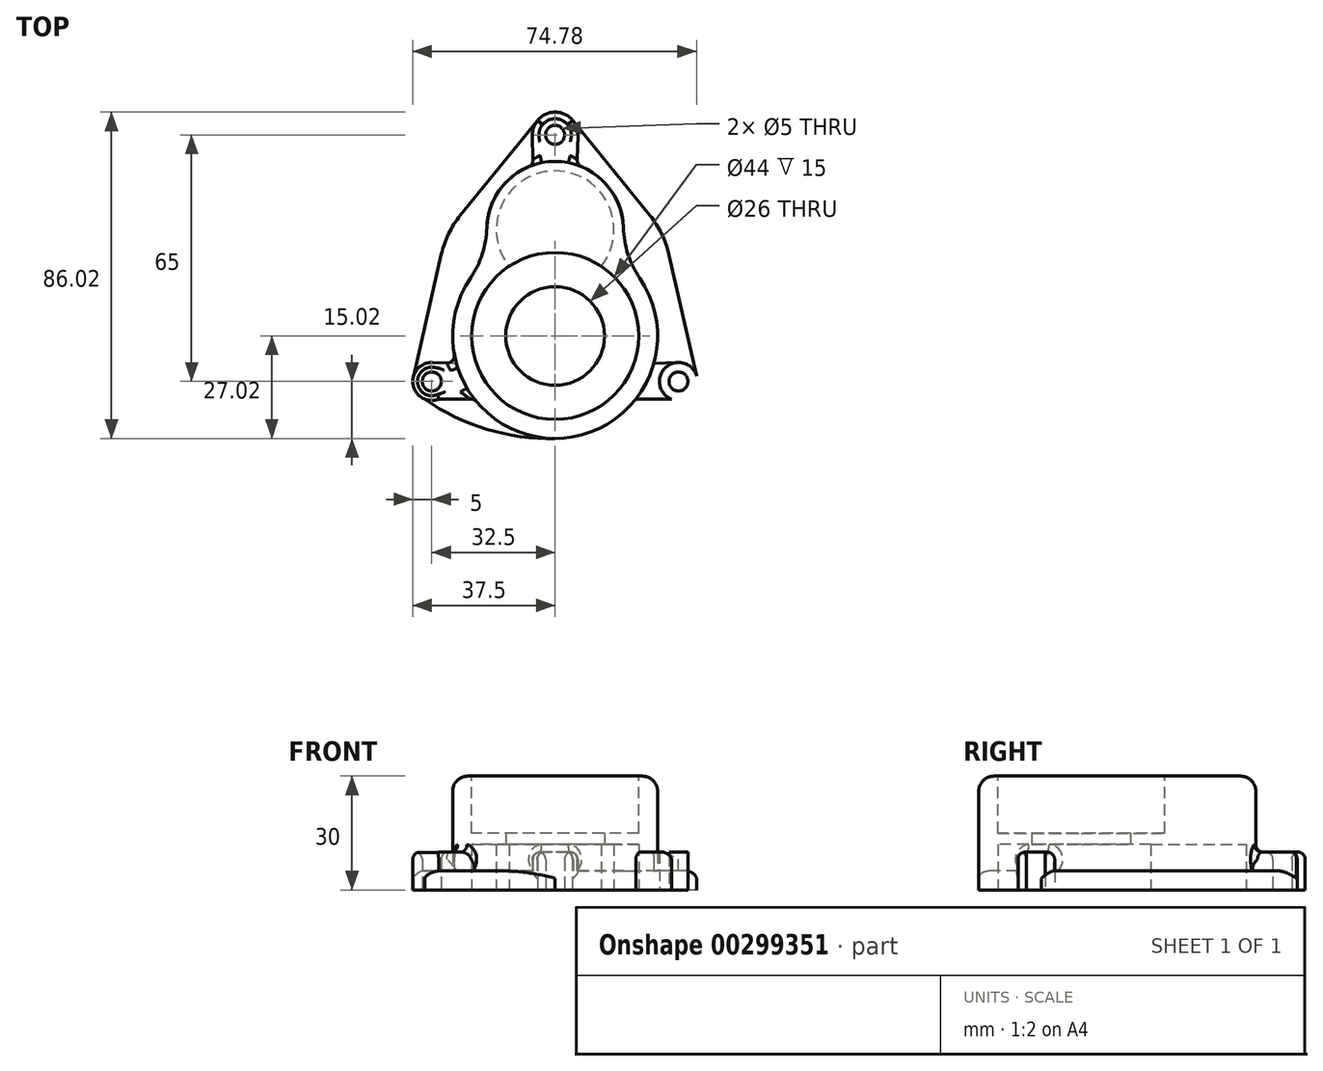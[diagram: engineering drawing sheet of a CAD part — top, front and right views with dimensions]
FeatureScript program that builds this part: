
annotation { "Feature Type Name" : "Feature", "Feature Type Description" : "" }
export const myFeature = defineFeature(function(context is Context, id is Id, definition is map)
    precondition{}
    {
        {
            var Q0;
            Q0=qCreatedBy(makeId("Top.planeOp"),FACE);
            var sketch = newSketch(context, id + "F0", { "sketchPlane" : qUnion([Q0])});
            skCircle(sketch, "E0", {"center": v(0, 0) * mm, "radius": 13 * mm});
            skCircle(sketch, "E1", {"center": v(0, 0) * mm, "radius": 22 * mm});
            skCircle(sketch, "E2", {"center": v(0, 0) * mm, "radius": 27 * mm});
            skPoint(sketch, "E3", {"position": v(32.5, -12) * mm});
            skPoint(sketch, "E4.MirrorP", {"position": v(-32.5, -12) * mm});
            skCircle(sketch, "E5", {"center": v(-32.5, -12) * mm, "radius": 2.5 * mm});
            skCircle(sketch, "E6.MirrorC", {"center": v(32.5, -12) * mm, "radius": 2.5 * mm});
            skPoint(sketch, "E7", {"position": v(0, 46) * mm});
            skPoint(sketch, "E8", {"position": v(0, 28) * mm});
            skLineSegment(sketch, "E9", {"start": v(-32.5, -12) * mm, "end": v(32.5, -12) * mm});
            skArc(sketch, "E10", {"start": v(16.68, 21.23) * mm, "mid": v(0, 46) * mm, "end": v(-16.68, 21.23) * mm});
            skCircle(sketch, "E11", {"center": v(0, 28) * mm, "radius": 15.5 * mm});
            skPoint(sketch, "E12", {"position": v(5.58, 15.98) * mm});
            skPoint(sketch, "E13", {"position": v(27.5, 28) * mm});
            skPoint(sketch, "E14.MirrorP", {"position": v(-5.58, 15.98) * mm});
            skPoint(sketch, "E15.MirrorP", {"position": v(-27.5, 28) * mm});
            skArc(sketch, "E16", {"start": v(29.95, 21.55) * mm, "mid": v(28.06, 26.93) * mm, "end": v(24.99, 31.74) * mm});
            skArc(sketch, "E17", {"start": v(-24.99, 31.74) * mm, "mid": v(-28.06, 26.93) * mm, "end": v(-29.95, 21.55) * mm});
            skPoint(sketch, "E18", {"position": v(0, 53) * mm});
            skCircle(sketch, "E19", {"center": v(0, 53) * mm, "radius": 6 * mm});
            skLineSegment(sketch, "E20", {"start": v(-6, 52.83) * mm, "end": v(-5.78, 45.05) * mm});
            skLineSegment(sketch, "E21.MirrorCS", {"start": v(6, 52.83) * mm, "end": v(5.78, 45.05) * mm});
            skLineSegment(sketch, "E22", {"start": v(-4.58, 56.88) * mm, "end": v(-24.99, 31.74) * mm});
            skLineSegment(sketch, "E23.MirrorCS", {"start": v(4.58, 56.88) * mm, "end": v(24.99, 31.74) * mm});
            skCircle(sketch, "E24", {"center": v(-32.5, -12) * mm, "radius": 5 * mm});
            skLineSegment(sketch, "E25", {"start": v(-37.28, -10.54) * mm, "end": v(-29.95, 21.55) * mm});
            skLineSegment(sketch, "E26.MirrorCS", {"start": v(37.28, -10.54) * mm, "end": v(29.95, 21.55) * mm});
            skCircle(sketch, "E27.MirrorC", {"center": v(32.5, -12) * mm, "radius": 5 * mm});
            skArc(sketch, "E28", {"start": v(-34.3, -16.66) * mm, "mid": v(-17.99, -24.6) * mm, "end": v(0, -27) * mm});
            skArc(sketch, "E29.MirrorCS", {"start": v(34.3, -16.66) * mm, "mid": v(17.99, -24.6) * mm, "end": v(0, -27) * mm});
            skCircle(sketch, "E30", {"center": v(0, 53) * mm, "radius": 2.5 * mm});
            skLineSegment(sketch, "E31", {"start": v(-32.34, -7) * mm, "end": v(-26.02, -7.2) * mm});
            skLineSegment(sketch, "E32", {"start": v(-34.3, -16.66) * mm, "end": v(-21.25, -16.66) * mm});
            skLineSegment(sketch, "E33.MirrorCS", {"start": v(32.34, -7) * mm, "end": v(26.02, -7.2) * mm});
            skLineSegment(sketch, "E34.MirrorCS", {"start": v(34.3, -16.66) * mm, "end": v(21.25, -16.66) * mm});
            skSolve(sketch);
        }
        {
            var Q0;
            {var subQ0=sQuery(id+"F0.wireOp",EDGE,"E11");var subQ1=sQuery(id+"F0.wireOp",EDGE,"E2");var subQ2=makeQuery(id+"F0.imprint","INTERSECT",VERTEX,{"disambiguationData":[OD(0.0)],"derivedFrom":[subQ1,subQ0]});Q0=makeQuery(id+"F0.imprint","IMPRINT",FACE,{"disambiguationData":[TD([[makeQuery(id+"F0.imprint","IMPRINT",EDGE,{"disambiguationData":[TD([[subQ2,-1.0]])],"derivedFrom":subQ1}),-1.0]])]});}
            var Q1;
            {var subQ0=sQuery(id+"F0.wireOp",EDGE,"E10");var subQ1=sQuery(id+"F0.wireOp",EDGE,"E2");var subQ2=makeQuery(id+"F0.imprint","INTERSECT",VERTEX,{"disambiguationData":[OD(0.0)],"derivedFrom":[subQ1,subQ0]});Q1=makeQuery(id+"F0.imprint","IMPRINT",FACE,{"disambiguationData":[TD([[makeQuery(id+"F0.imprint","IMPRINT",EDGE,{"disambiguationData":[TD([[subQ2,-1.0]])],"derivedFrom":subQ1}),-1.0]])]});}
            var Q2;
            {var subQ0=sQuery(id+"F0.wireOp",EDGE,"E11");var subQ1=sQuery(id+"F0.wireOp",EDGE,"E1");var subQ2=makeQuery(id+"F0.imprint","INTERSECT",VERTEX,{"disambiguationData":[OD(0.0)],"derivedFrom":[subQ1,subQ0]});Q2=makeQuery(id+"F0.imprint","IMPRINT",FACE,{"disambiguationData":[TD([[makeQuery(id+"F0.imprint","IMPRINT",EDGE,{"disambiguationData":[TD([[subQ2,1.0]])],"derivedFrom":subQ1}),-1.0]])]});}
            var Q3;
            {var subQ0=sQuery(id+"F0.wireOp",EDGE,"E11");var subQ1=sQuery(id+"F0.wireOp",EDGE,"E0");var subQ2=makeQuery(id+"F0.imprint","INTERSECT",VERTEX,{"disambiguationData":[OD(0.0)],"derivedFrom":[subQ1,subQ0]});Q3=makeQuery(id+"F0.imprint","IMPRINT",FACE,{"disambiguationData":[TD([[makeQuery(id+"F0.imprint","IMPRINT",EDGE,{"disambiguationData":[TD([[subQ2,1.0]])],"derivedFrom":subQ1}),-1.0]])]});}
            var Q4;
            {var subQ4=sQuery(id+"F0.wireOp",EDGE,"E11");var subQ6=sQuery(id+"F0.wireOp",EDGE,"E1");var subQ8=makeQuery(id+"F0.imprint","INTERSECT",VERTEX,{"disambiguationData":[OD(1.0)],"derivedFrom":[subQ6,subQ4]});Q4=makeQuery(id+"F0.imprint","IMPRINT",FACE,{"disambiguationData":[TD([[makeQuery(id+"F0.imprint","IMPRINT",EDGE,{"disambiguationData":[TD([[subQ8,1.0]])],"derivedFrom":subQ6}),-1.0]])]});}
            var Q5;
            {var subQ1=sQuery(id+"F0.wireOp",EDGE,"E1");var subQ6=sQuery(id+"F0.wireOp",EDGE,"E11");var subQ8=makeQuery(id+"F0.imprint","INTERSECT",VERTEX,{"disambiguationData":[OD(0.0)],"derivedFrom":[subQ1,subQ6]});Q5=makeQuery(id+"F0.imprint","IMPRINT",FACE,{"disambiguationData":[TD([[makeQuery(id+"F0.imprint","IMPRINT",EDGE,{"disambiguationData":[TD([[subQ8,-1.0]])],"derivedFrom":subQ1}),-1.0]])]});}
            var Q6;
            {var subQ0=sQuery(id+"F0.wireOp",EDGE,"E11");var subQ1=sQuery(id+"F0.wireOp",EDGE,"E0");var subQ2=makeQuery(id+"F0.imprint","INTERSECT",VERTEX,{"disambiguationData":[OD(0.0)],"derivedFrom":[subQ1,subQ0]});Q6=makeQuery(id+"F0.imprint","IMPRINT",FACE,{"disambiguationData":[TD([[makeQuery(id+"F0.imprint","IMPRINT",EDGE,{"disambiguationData":[TD([[subQ2,-1.0]])],"derivedFrom":subQ1}),-1.0]])]});}
            var Q7;
            {var subQ0=sQuery(id+"F0.wireOp",EDGE,"E11");var subQ1=sQuery(id+"F0.wireOp",EDGE,"E0");var subQ2=makeQuery(id+"F0.imprint","INTERSECT",VERTEX,{"disambiguationData":[OD(1.0)],"derivedFrom":[subQ1,subQ0]});Q7=makeQuery(id+"F0.imprint","IMPRINT",FACE,{"disambiguationData":[TD([[makeQuery(id+"F0.imprint","IMPRINT",EDGE,{"disambiguationData":[TD([[subQ2,1.0]])],"derivedFrom":subQ1}),-1.0]])]});}
            var Q8;
            {var subQ0=sQuery(id+"F0.wireOp",EDGE,"E11");var subQ1=sQuery(id+"F0.wireOp",EDGE,"E0");var subQ2=makeQuery(id+"F0.imprint","INTERSECT",VERTEX,{"disambiguationData":[OD(0.0)],"derivedFrom":[subQ1,subQ0]});Q8=makeQuery(id+"F0.imprint","IMPRINT",FACE,{"disambiguationData":[TD([[makeQuery(id+"F0.imprint","IMPRINT",EDGE,{"disambiguationData":[TD([[subQ2,-1.0]])],"derivedFrom":subQ1}),1.0]])]});}
            var Q9;
            {var subQ0=sQuery(id+"F0.wireOp",EDGE,"E9");var subQ1=sQuery(id+"F0.wireOp",EDGE,"E0");var subQ2=makeQuery(id+"F0.imprint","INTERSECT",VERTEX,{"disambiguationData":[OD(0.0)],"derivedFrom":[subQ1,subQ0]});Q9=makeQuery(id+"F0.imprint","IMPRINT",FACE,{"disambiguationData":[TD([[makeQuery(id+"F0.imprint","IMPRINT",EDGE,{"disambiguationData":[TD([[subQ2,-1.0]])],"derivedFrom":subQ1}),-1.0]])]});}
            var Q10;
            {var subQ0=sQuery(id+"F0.wireOp",EDGE,"E9");var subQ1=sQuery(id+"F0.wireOp",EDGE,"E1");var subQ2=makeQuery(id+"F0.imprint","INTERSECT",VERTEX,{"disambiguationData":[OD(0.0)],"derivedFrom":[subQ1,subQ0]});Q10=makeQuery(id+"F0.imprint","IMPRINT",FACE,{"disambiguationData":[TD([[makeQuery(id+"F0.imprint","IMPRINT",EDGE,{"disambiguationData":[TD([[subQ2,-1.0]])],"derivedFrom":subQ1}),-1.0]])]});}
            var Q11;
            {var subQ0=sQuery(id+"F0.wireOp",EDGE,"E9");var subQ1=sQuery(id+"F0.wireOp",EDGE,"E0");var subQ2=makeQuery(id+"F0.imprint","INTERSECT",VERTEX,{"disambiguationData":[OD(0.0)],"derivedFrom":[subQ1,subQ0]});Q11=makeQuery(id+"F0.imprint","IMPRINT",FACE,{"disambiguationData":[TD([[makeQuery(id+"F0.imprint","IMPRINT",EDGE,{"disambiguationData":[TD([[subQ2,-1.0]])],"derivedFrom":subQ1}),1.0]])]});}
            var Q12;
            {var subQ0=sQuery(id+"F0.wireOp",EDGE,"E11");var subQ1=sQuery(id+"F0.wireOp",EDGE,"E0");var subQ2=makeQuery(id+"F0.imprint","INTERSECT",VERTEX,{"disambiguationData":[OD(0.0)],"derivedFrom":[subQ1,subQ0]});Q12=makeQuery(id+"F0.imprint","IMPRINT",FACE,{"disambiguationData":[TD([[makeQuery(id+"F0.imprint","IMPRINT",EDGE,{"disambiguationData":[TD([[subQ2,1.0]])],"derivedFrom":subQ1}),1.0]])]});}
            extrude(context, id + "F1", {"entities" : qUnion([Q0, Q1, Q2, Q3, Q4, Q5, Q6, Q7, Q8, Q9, Q10, Q11, Q12]), "depth" : 30 * mm});
        }
        {
            var Q0;
            {var subQ0=sQuery(id+"F0.wireOp",EDGE,"E10");var subQ1=sQuery(id+"F0.wireOp",EDGE,"E2");Q0=makeQuery(id+"F1.opExtrude","SWEPT_EDGE",EDGE,{"disambiguationData":[OSD([subQ1,subQ0]),TDD([makeQuery(id+"F0.imprint","INTERSECT",VERTEX,{"disambiguationData":[OD(1.0)],"derivedFrom":[subQ1,subQ0]})])]});}
            var Q1;
            {var subQ0=sQuery(id+"F0.wireOp",EDGE,"E10");var subQ1=sQuery(id+"F0.wireOp",EDGE,"E2");Q1=makeQuery(id+"F1.opExtrude","SWEPT_EDGE",EDGE,{"disambiguationData":[OSD([subQ1,subQ0]),TDD([makeQuery(id+"F0.imprint","INTERSECT",VERTEX,{"disambiguationData":[OD(0.0)],"derivedFrom":[subQ1,subQ0]})])]});}
            fillet(context, id + "F2", {"entities" : qUnion([Q0, Q1]), "radius" : 25 * mm, "tangentPropagation" : true, "allowEdgeOverflow" : false});
        }
        {
            var Q0;
            Q0=makeQuery(id+"F0.imprint","IMPRINT",FACE,{"disambiguationData":[TD([[makeQuery(id+"F0.imprint","IMPRINT",EDGE,{"derivedFrom":sQuery(id+"F0.wireOp",EDGE,"E5")}),-1.0]])]});
            var Q1;
            {var subQ0=sQuery(id+"F0.wireOp",EDGE,"E32");var subQ1=sQuery(id+"F0.wireOp",EDGE,"E2");var subQ2=makeQuery(id+"F0.imprint","INTERSECT",VERTEX,{"derivedFrom":[subQ1,subQ0]});Q1=makeQuery(id+"F0.imprint","IMPRINT",FACE,{"disambiguationData":[TD([[makeQuery(id+"F0.imprint","IMPRINT",EDGE,{"disambiguationData":[TD([[subQ2,1.0]])],"derivedFrom":subQ1}),-1.0]])]});}
            var Q2;
            {var subQ0=sQuery(id+"F0.wireOp",EDGE,"E31");Q2=makeQuery(id+"F0.imprint","IMPRINT",FACE,{"disambiguationData":[TD([[makeQuery(id+"F0.imprint","IMPRINT",EDGE,{"derivedFrom":subQ0}),-1.0]])]});}
            var Q3;
            {var subQ0=sQuery(id+"F0.wireOp",EDGE,"E34.MirrorCS");var subQ1=sQuery(id+"F0.wireOp",EDGE,"E2");var subQ2=makeQuery(id+"F0.imprint","INTERSECT",VERTEX,{"derivedFrom":[subQ1,subQ0]});Q3=makeQuery(id+"F0.imprint","IMPRINT",FACE,{"disambiguationData":[TD([[makeQuery(id+"F0.imprint","IMPRINT",EDGE,{"disambiguationData":[TD([[subQ2,-1.0]])],"derivedFrom":subQ1}),-1.0]])]});}
            var Q4;
            {var subQ0=sQuery(id+"F0.wireOp",EDGE,"E33.MirrorCS");Q4=makeQuery(id+"F0.imprint","IMPRINT",FACE,{"disambiguationData":[TD([[makeQuery(id+"F0.imprint","IMPRINT",EDGE,{"derivedFrom":subQ0}),1.0]])]});}
            var Q5;
            Q5=makeQuery(id+"F0.imprint","IMPRINT",FACE,{"disambiguationData":[TD([[makeQuery(id+"F0.imprint","IMPRINT",EDGE,{"derivedFrom":sQuery(id+"F0.wireOp",EDGE,"E6.MirrorC")}),1.0]])]});
            var Q6;
            {var subQ0=sQuery(id+"F0.wireOp",EDGE,"E20");Q6=makeQuery(id+"F0.imprint","IMPRINT",FACE,{"disambiguationData":[TD([[makeQuery(id+"F0.imprint","IMPRINT",EDGE,{"derivedFrom":subQ0}),1.0]])]});}
            var Q7;
            Q7=makeQuery(id+"F0.imprint","IMPRINT",FACE,{"disambiguationData":[TD([[makeQuery(id+"F0.imprint","IMPRINT",EDGE,{"derivedFrom":sQuery(id+"F0.wireOp",EDGE,"E30")}),-1.0]])]});
            var Q8;
            {var subQ0=sQuery(id+"F0.wireOp",EDGE,"E32");var subQ1=sQuery(id+"F0.wireOp",EDGE,"E24");var subQ3=makeQuery(id+"F0.imprint","INTERSECT",VERTEX,{"derivedFrom":[subQ1,subQ0]});Q8=makeQuery(id+"F0.imprint","IMPRINT",FACE,{"disambiguationData":[TD([[makeQuery(id+"F0.imprint","IMPRINT",EDGE,{"disambiguationData":[TD([[subQ3,1.0]])],"derivedFrom":subQ1}),1.0]])]});}
            var Q9;
            {var subQ0=sQuery(id+"F0.wireOp",EDGE,"E34.MirrorCS");var subQ1=sQuery(id+"F0.wireOp",EDGE,"E27.MirrorC");var subQ3=makeQuery(id+"F0.imprint","INTERSECT",VERTEX,{"derivedFrom":[subQ1,subQ0]});Q9=makeQuery(id+"F0.imprint","IMPRINT",FACE,{"disambiguationData":[TD([[makeQuery(id+"F0.imprint","IMPRINT",EDGE,{"disambiguationData":[TD([[subQ3,1.0]])],"derivedFrom":subQ1}),-1.0]])]});}
            extrude(context, id + "F3", {"entities" : qUnion([Q0, Q1, Q2, Q3, Q4, Q5, Q6, Q7, Q8, Q9]), "operationType" : NewBodyOperationType.ADD, "depth" : 10 * mm});
        }
        {
            var Q0;
            {var subQ4=sQuery(id+"F0.wireOp",EDGE,"E17");Q0=makeQuery(id+"F0.imprint","IMPRINT",FACE,{"disambiguationData":[TD([[makeQuery(id+"F0.imprint","IMPRINT",EDGE,{"derivedFrom":subQ4}),1.0]])]});}
            var Q1;
            {var subQ4=sQuery(id+"F0.wireOp",EDGE,"E16");Q1=makeQuery(id+"F0.imprint","IMPRINT",FACE,{"disambiguationData":[TD([[makeQuery(id+"F0.imprint","IMPRINT",EDGE,{"derivedFrom":subQ4}),1.0]])]});}
            var Q2;
            {var subQ0=sQuery(id+"F0.wireOp",EDGE,"E28");Q2=makeQuery(id+"F0.imprint","IMPRINT",FACE,{"disambiguationData":[TD([[makeQuery(id+"F0.imprint","IMPRINT",EDGE,{"derivedFrom":subQ0}),1.0]])]});}
            var Q3;
            {var subQ0=sQuery(id+"F0.wireOp",EDGE,"E29.MirrorCS");Q3=makeQuery(id+"F0.imprint","IMPRINT",FACE,{"disambiguationData":[TD([[makeQuery(id+"F0.imprint","IMPRINT",EDGE,{"derivedFrom":subQ0}),-1.0]])]});}
            extrude(context, id + "F4", {"entities" : qUnion([Q0, Q1, Q2, Q3]), "operationType" : NewBodyOperationType.ADD, "depth" : 5 * mm});
        }
        {
            var Q0;
            {var subQ0=sQuery(id+"F0.wireOp",EDGE,"E11");var subQ1=sQuery(id+"F0.wireOp",EDGE,"E1");var subQ2=makeQuery(id+"F0.imprint","INTERSECT",VERTEX,{"disambiguationData":[OD(0.0)],"derivedFrom":[subQ1,subQ0]});Q0=makeQuery(id+"F0.imprint","IMPRINT",FACE,{"disambiguationData":[TD([[makeQuery(id+"F0.imprint","IMPRINT",EDGE,{"disambiguationData":[TD([[subQ2,1.0]])],"derivedFrom":subQ1}),-1.0]])]});}
            var Q1;
            {var subQ0=sQuery(id+"F0.wireOp",EDGE,"E11");var subQ1=sQuery(id+"F0.wireOp",EDGE,"E2");var subQ2=makeQuery(id+"F0.imprint","INTERSECT",VERTEX,{"disambiguationData":[OD(0.0)],"derivedFrom":[subQ1,subQ0]});Q1=makeQuery(id+"F0.imprint","IMPRINT",FACE,{"disambiguationData":[TD([[makeQuery(id+"F0.imprint","IMPRINT",EDGE,{"disambiguationData":[TD([[subQ2,-1.0]])],"derivedFrom":subQ1}),-1.0]])]});}
            var Q2;
            {var subQ0=sQuery(id+"F0.wireOp",EDGE,"E11");var subQ1=sQuery(id+"F0.wireOp",EDGE,"E0");var subQ2=makeQuery(id+"F0.imprint","INTERSECT",VERTEX,{"disambiguationData":[OD(0.0)],"derivedFrom":[subQ1,subQ0]});Q2=makeQuery(id+"F0.imprint","IMPRINT",FACE,{"disambiguationData":[TD([[makeQuery(id+"F0.imprint","IMPRINT",EDGE,{"disambiguationData":[TD([[subQ2,1.0]])],"derivedFrom":subQ1}),-1.0]])]});}
            var Q3;
            {var subQ0=sQuery(id+"F0.wireOp",EDGE,"E11");var subQ1=sQuery(id+"F0.wireOp",EDGE,"E0");var subQ2=makeQuery(id+"F0.imprint","INTERSECT",VERTEX,{"disambiguationData":[OD(0.0)],"derivedFrom":[subQ1,subQ0]});Q3=makeQuery(id+"F0.imprint","IMPRINT",FACE,{"disambiguationData":[TD([[makeQuery(id+"F0.imprint","IMPRINT",EDGE,{"disambiguationData":[TD([[subQ2,-1.0]])],"derivedFrom":subQ1}),-1.0]])]});}
            var Q4;
            {var subQ0=sQuery(id+"F0.wireOp",EDGE,"E9");var subQ1=sQuery(id+"F0.wireOp",EDGE,"E0");var subQ2=makeQuery(id+"F0.imprint","INTERSECT",VERTEX,{"disambiguationData":[OD(0.0)],"derivedFrom":[subQ1,subQ0]});Q4=makeQuery(id+"F0.imprint","IMPRINT",FACE,{"disambiguationData":[TD([[makeQuery(id+"F0.imprint","IMPRINT",EDGE,{"disambiguationData":[TD([[subQ2,-1.0]])],"derivedFrom":subQ1}),-1.0]])]});}
            var Q5;
            {var subQ0=sQuery(id+"F0.wireOp",EDGE,"E11");var subQ1=sQuery(id+"F0.wireOp",EDGE,"E0");var subQ2=makeQuery(id+"F0.imprint","INTERSECT",VERTEX,{"disambiguationData":[OD(1.0)],"derivedFrom":[subQ1,subQ0]});Q5=makeQuery(id+"F0.imprint","IMPRINT",FACE,{"disambiguationData":[TD([[makeQuery(id+"F0.imprint","IMPRINT",EDGE,{"disambiguationData":[TD([[subQ2,1.0]])],"derivedFrom":subQ1}),-1.0]])]});}
            var Q6;
            {var subQ0=sQuery(id+"F0.wireOp",EDGE,"E11");var subQ1=sQuery(id+"F0.wireOp",EDGE,"E0");var subQ2=makeQuery(id+"F0.imprint","INTERSECT",VERTEX,{"disambiguationData":[OD(0.0)],"derivedFrom":[subQ1,subQ0]});Q6=makeQuery(id+"F0.imprint","IMPRINT",FACE,{"disambiguationData":[TD([[makeQuery(id+"F0.imprint","IMPRINT",EDGE,{"disambiguationData":[TD([[subQ2,-1.0]])],"derivedFrom":subQ1}),1.0]])]});}
            var Q7;
            {var subQ0=sQuery(id+"F0.wireOp",EDGE,"E11");var subQ1=sQuery(id+"F0.wireOp",EDGE,"E0");var subQ2=makeQuery(id+"F0.imprint","INTERSECT",VERTEX,{"disambiguationData":[OD(0.0)],"derivedFrom":[subQ1,subQ0]});Q7=makeQuery(id+"F0.imprint","IMPRINT",FACE,{"disambiguationData":[TD([[makeQuery(id+"F0.imprint","IMPRINT",EDGE,{"disambiguationData":[TD([[subQ2,1.0]])],"derivedFrom":subQ1}),1.0]])]});}
            var Q8;
            {var subQ0=sQuery(id+"F0.wireOp",EDGE,"E9");var subQ1=sQuery(id+"F0.wireOp",EDGE,"E0");var subQ2=makeQuery(id+"F0.imprint","INTERSECT",VERTEX,{"disambiguationData":[OD(0.0)],"derivedFrom":[subQ1,subQ0]});Q8=makeQuery(id+"F0.imprint","IMPRINT",FACE,{"disambiguationData":[TD([[makeQuery(id+"F0.imprint","IMPRINT",EDGE,{"disambiguationData":[TD([[subQ2,-1.0]])],"derivedFrom":subQ1}),1.0]])]});}
            extrude(context, id + "F5", {"entities" : qUnion([Q0, Q1, Q2, Q3, Q4, Q5, Q6, Q7, Q8]), "operationType" : NewBodyOperationType.REMOVE, "depth" : 12 * mm});
        }
        {
            var Q0;
            Q0=makeQuery(id+"F1.opExtrude","CAP_FACE",FACE,{"disambiguationData":[OSD([sQuery(id+"F0.wireOp",EDGE,"E2"),sQuery(id+"F0.wireOp",EDGE,"E10")])],"isStart":false});
            var sketch = newSketch(context, id + "F6", { "sketchPlane" : qUnion([Q0])});
            skCircle(sketch, "E35.0", {"center": v(0, 0) * mm, "radius": 22 * mm});
            skSolve(sketch);
        }
        {
            var Q0;
            Q0=makeQuery(id+"F6.imprint","IMPRINT",FACE,{"disambiguationData":[TD([[makeQuery(id+"F6.imprint","IMPRINT",EDGE,{"derivedFrom":sQuery(id+"F6.wireOp",EDGE,"E35.0")}),1.0]])]});
            extrude(context, id + "F7", {"entities" : qUnion([Q0]), "operationType" : NewBodyOperationType.REMOVE, "oppositeDirection" : true, "depth" : 15 * mm});
        }
        {
            var Q0;
            {var subQ0=sQuery(id+"F0.wireOp",EDGE,"E11");var subQ1=sQuery(id+"F0.wireOp",EDGE,"E0");var subQ2=makeQuery(id+"F0.imprint","INTERSECT",VERTEX,{"disambiguationData":[OD(0.0)],"derivedFrom":[subQ1,subQ0]});Q0=makeQuery(id+"F0.imprint","IMPRINT",FACE,{"disambiguationData":[TD([[makeQuery(id+"F0.imprint","IMPRINT",EDGE,{"disambiguationData":[TD([[subQ2,-1.0]])],"derivedFrom":subQ1}),1.0]])]});}
            var Q1;
            {var subQ0=sQuery(id+"F0.wireOp",EDGE,"E11");var subQ1=sQuery(id+"F0.wireOp",EDGE,"E0");var subQ2=makeQuery(id+"F0.imprint","INTERSECT",VERTEX,{"disambiguationData":[OD(0.0)],"derivedFrom":[subQ1,subQ0]});Q1=makeQuery(id+"F0.imprint","IMPRINT",FACE,{"disambiguationData":[TD([[makeQuery(id+"F0.imprint","IMPRINT",EDGE,{"disambiguationData":[TD([[subQ2,1.0]])],"derivedFrom":subQ1}),1.0]])]});}
            var Q2;
            {var subQ0=sQuery(id+"F0.wireOp",EDGE,"E9");var subQ1=sQuery(id+"F0.wireOp",EDGE,"E0");var subQ2=makeQuery(id+"F0.imprint","INTERSECT",VERTEX,{"disambiguationData":[OD(0.0)],"derivedFrom":[subQ1,subQ0]});Q2=makeQuery(id+"F0.imprint","IMPRINT",FACE,{"disambiguationData":[TD([[makeQuery(id+"F0.imprint","IMPRINT",EDGE,{"disambiguationData":[TD([[subQ2,-1.0]])],"derivedFrom":subQ1}),1.0]])]});}
            extrude(context, id + "F8", {"entities" : qUnion([Q0, Q1, Q2]), "operationType" : NewBodyOperationType.REMOVE, "endBound" : BoundingType.THROUGH_ALL, "depth" : 25 * mm});
        }
        {
            var Q0;
            Q0=makeQuery(id+"F1.opExtrude","CAP_EDGE",EDGE,{"disambiguationData":[OSD([sQuery(id+"F0.wireOp",EDGE,"E2")])],"isStart":false});
            fillet(context, id + "F9", {"entities" : qUnion([Q0]), "radius" : 4 * mm, "tangentPropagation" : true, "allowEdgeOverflow" : false});
        }
        {
            var Q0;
            Q0=makeQuery(id+"F3.opExtrude","CAP_EDGE",EDGE,{"disambiguationData":[OSD([sQuery(id+"F0.wireOp",EDGE,"E34.MirrorCS")])],"isStart":false});
            var Q1;
            Q1=makeQuery(id+"F3.opExtrude","CAP_EDGE",EDGE,{"disambiguationData":[OSD([sQuery(id+"F0.wireOp",EDGE,"E33.MirrorCS")])],"isStart":false});
            fillet(context, id + "F10", {"entities" : qUnion([Q0, Q1]), "radius" : 1.93 * mm, "tangentPropagation" : true, "allowEdgeOverflow" : false});
        }
        {
            var Q0;
            Q0=makeQuery(id+"F3.opExtrude","CAP_FACE",FACE,{"disambiguationData":[OSD([sQuery(id+"F0.wireOp",EDGE,"E2"),sQuery(id+"F0.wireOp",EDGE,"E5"),sQuery(id+"F0.wireOp",EDGE,"E24"),sQuery(id+"F0.wireOp",EDGE,"E31"),sQuery(id+"F0.wireOp",EDGE,"E32")])],"isStart":false});
            var Q1;
            Q1=makeQuery(id+"F3.opExtrude","SWEPT_EDGE",EDGE,{"disambiguationData":[OSD([sQuery(id+"F0.wireOp",EDGE,"E2"),sQuery(id+"F0.wireOp",EDGE,"E31")])]});
            var Q2;
            Q2=makeQuery(id+"F3.opExtrude","SWEPT_EDGE",EDGE,{"disambiguationData":[OSD([sQuery(id+"F0.wireOp",EDGE,"E2"),sQuery(id+"F0.wireOp",EDGE,"E32")])]});
            fillet(context, id + "F11", {"entities" : qUnion([Q0, Q1, Q2]), "radius" : 1.93 * mm, "tangentPropagation" : true, "allowEdgeOverflow" : false});
        }
        {
            var Q0;
            Q0=makeQuery(id+"F3.opExtrude","CAP_FACE",FACE,{"disambiguationData":[OSD([sQuery(id+"F0.wireOp",EDGE,"E10"),sQuery(id+"F0.wireOp",EDGE,"E19"),sQuery(id+"F0.wireOp",EDGE,"E20"),sQuery(id+"F0.wireOp",EDGE,"E21.MirrorCS"),sQuery(id+"F0.wireOp",EDGE,"E22"),sQuery(id+"F0.wireOp",EDGE,"E23.MirrorCS"),sQuery(id+"F0.wireOp",EDGE,"E30")])],"isStart":false});
            fillet(context, id + "F12", {"entities" : qUnion([Q0]), "radius" : 1.93 * mm, "tangentPropagation" : true, "allowEdgeOverflow" : false});
        }
        {
            var Q0;
            Q0=makeQuery(id+"F4.opExtrude","CAP_EDGE",EDGE,{"disambiguationData":[OSD([sQuery(id+"F0.wireOp",EDGE,"E28")])],"isStart":false});
            var Q1;
            Q1=makeQuery(id+"F4.opExtrude","CAP_EDGE",EDGE,{"disambiguationData":[OSD([sQuery(id+"F0.wireOp",EDGE,"E29.MirrorCS")])],"isStart":false});
            fillet(context, id + "F13", {"entities" : qUnion([Q0, Q1]), "radius" : 2 * mm, "tangentPropagation" : true, "allowEdgeOverflow" : false});
        }
        {
            var Q0;
            Q0=makeQuery(id+"F4.opExtrude","CAP_EDGE",EDGE,{"disambiguationData":[OSD([sQuery(id+"F0.wireOp",EDGE,"E23.MirrorCS")])],"isStart":false});
            var Q1;
            Q1=makeQuery(id+"F4.opExtrude","CAP_EDGE",EDGE,{"disambiguationData":[OSD([sQuery(id+"F0.wireOp",EDGE,"E16")])],"isStart":false});
            var Q2;
            Q2=makeQuery(id+"F4.opExtrude","CAP_EDGE",EDGE,{"disambiguationData":[OSD([sQuery(id+"F0.wireOp",EDGE,"E26.MirrorCS")])],"isStart":false});
            fillet(context, id + "F14", {"entities" : qUnion([Q0, Q1, Q2]), "radius" : 2 * mm, "tangentPropagation" : true, "allowEdgeOverflow" : false});
        }
        {
            var Q0;
            Q0=makeQuery(id+"F4.opExtrude","CAP_EDGE",EDGE,{"disambiguationData":[OSD([sQuery(id+"F0.wireOp",EDGE,"E22")])],"isStart":false});
            var Q1;
            Q1=makeQuery(id+"F4.opExtrude","CAP_EDGE",EDGE,{"disambiguationData":[OSD([sQuery(id+"F0.wireOp",EDGE,"E17")])],"isStart":false});
            var Q2;
            Q2=makeQuery(id+"F4.opExtrude","CAP_EDGE",EDGE,{"disambiguationData":[OSD([sQuery(id+"F0.wireOp",EDGE,"E25")])],"isStart":false});
            fillet(context, id + "F15", {"entities" : qUnion([Q0, Q1, Q2]), "radius" : 2 * mm, "tangentPropagation" : true, "allowEdgeOverflow" : false});
        }
    });
